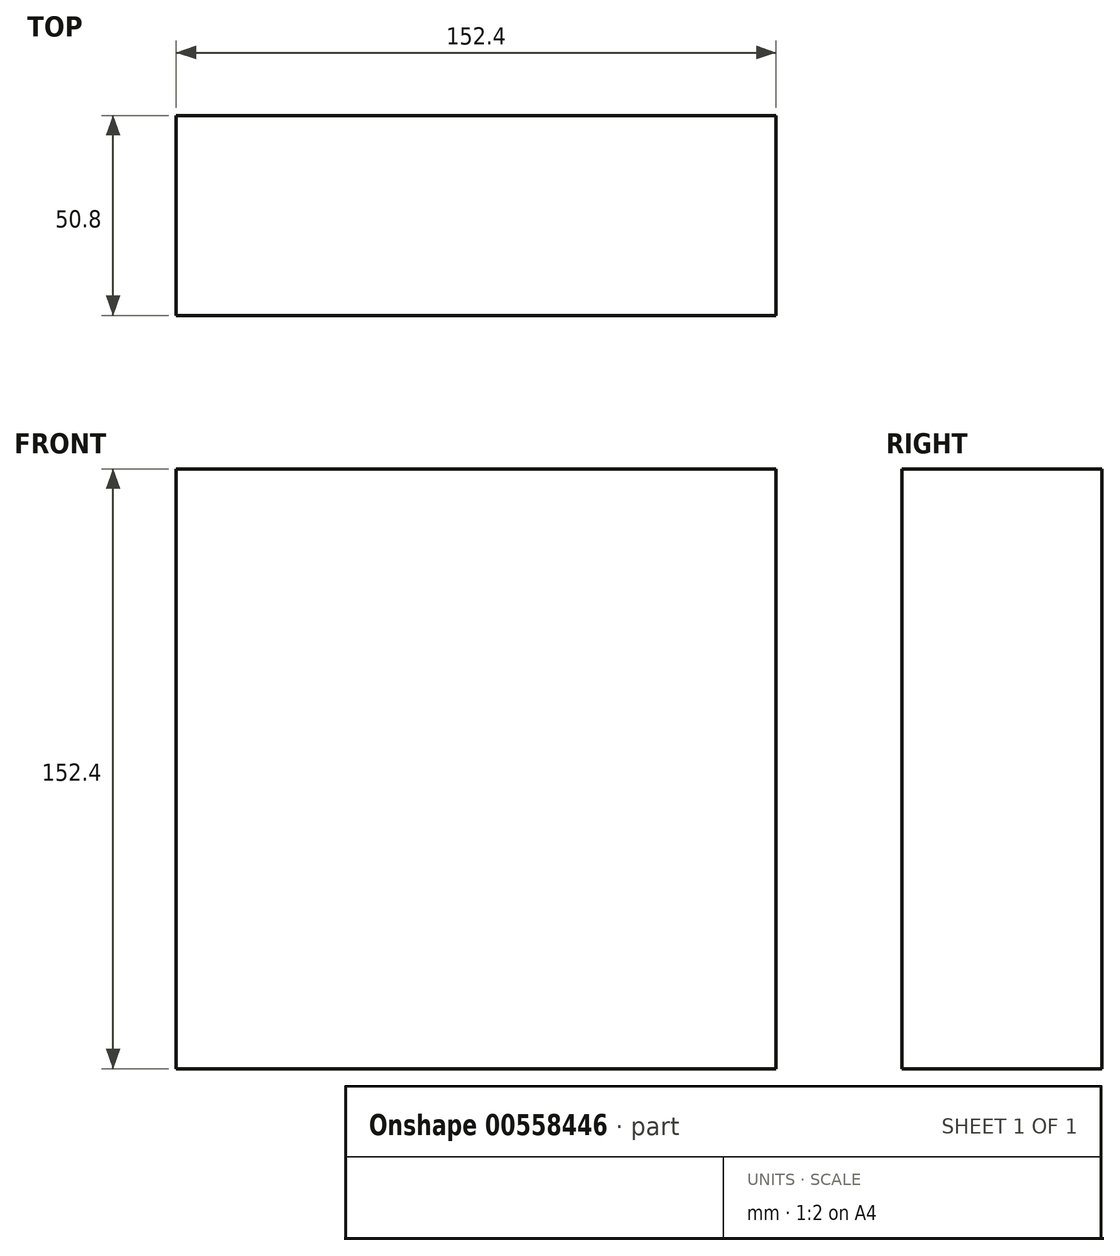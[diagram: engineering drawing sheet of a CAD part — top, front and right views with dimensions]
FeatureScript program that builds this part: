
annotation { "Feature Type Name" : "Feature", "Feature Type Description" : "" }
export const myFeature = defineFeature(function(context is Context, id is Id, definition is map)
    precondition{}
    {
        {
            var Q0;
            Q0=qCreatedBy(makeId("Front.planeOp"),FACE);
            var sketch = newSketch(context, id + "F0", { "sketchPlane" : qUnion([Q0])});
            skLineSegment(sketch, "E0.bottom", {"start": v(0, 0) * mm, "end": v(152.4, 0) * mm});
            skLineSegment(sketch, "E0.top", {"start": v(0, 152.4) * mm, "end": v(152.4, 152.4) * mm});
            skLineSegment(sketch, "E0.left", {"start": v(0, 0) * mm, "end": v(0, 152.4) * mm});
            skLineSegment(sketch, "E0.right", {"start": v(152.4, 0) * mm, "end": v(152.4, 152.4) * mm});
            skSolve(sketch);
        }
        {
            var Q0;
            Q0 = qSketchRegion(id + "F0", true);
            extrude(context, id + "F1", {"entities" : qUnion([Q0]), "depth" : 50.8 * mm, "offsetDistance" : 25.4 * mm});
        }
    });
